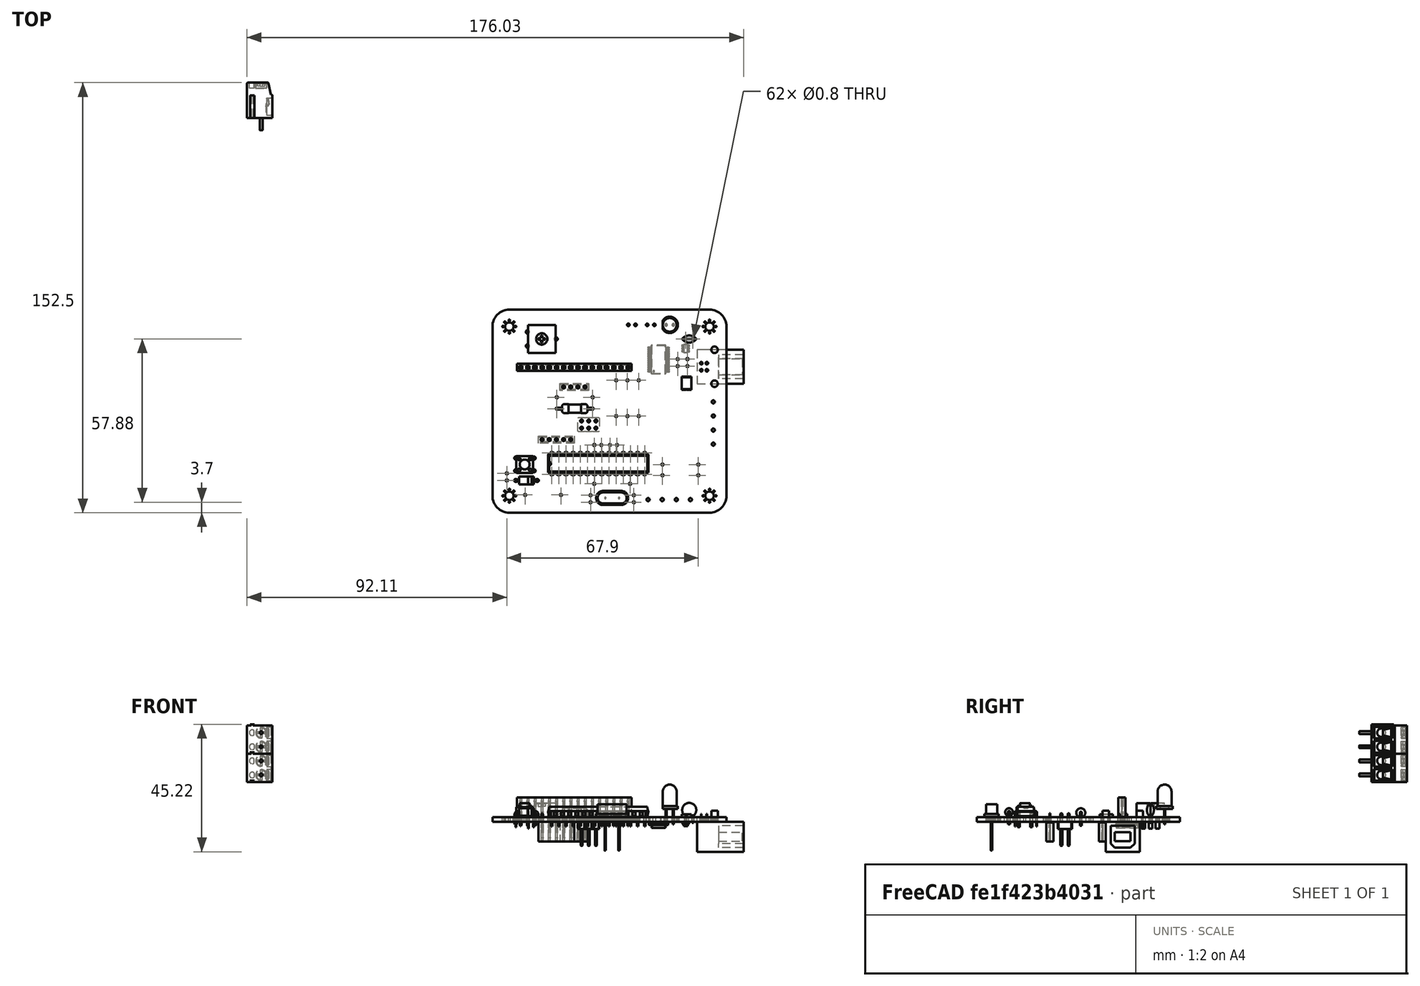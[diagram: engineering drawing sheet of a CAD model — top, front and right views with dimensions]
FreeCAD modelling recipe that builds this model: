
FCSTD DOCUMENT  (FreeCAD 0.19R22665 (Git))
Label: pcb_board
License: All rights reserved
LicenseURL: http://en.wikipedia.org/wiki/All_rights_reserved
objects: App::Link×20, Part::Feature×19, App::Part×6, PartDesign::CoordinateSystem×3, Sketcher::SketchObject×1
note: 23 computed .brp shape members not serialized (recipe doc carries the construction recipe); baked Part::Feature solids carry a one-line shape summary decoded from their .brp

FEATURE [PartDesign::CoordinateSystem] Local_CS_8929
  AttacherType = Attacher::AttachEngine3D
FEATURE [Part::Feature] Pcb_8929
  shape: bbox 83 x 72 x 1.6 mm, 170 faces (baked)
FEATURE [Sketcher::SketchObject] PCB_Sketch_8929
  sketch-geometry (8):
    g0: LineSegment StartX=93 StartY=-68 StartZ=0 EndX=164 EndY=-68 EndZ=0
    g1: LineSegment StartX=170 StartY=-134 StartZ=0 EndX=170 EndY=-74 EndZ=0
    g2: LineSegment StartX=93 StartY=-140 StartZ=0 EndX=164 EndY=-140 EndZ=0
    g3: LineSegment StartX=87 StartY=-74 StartZ=0 EndX=87 EndY=-134 EndZ=0
    g4: ArcOfCircle CenterX=164 CenterY=-74 CenterZ=0 NormalX=0 NormalY=0 NormalZ=1 AngleXU=0 Radius=6 StartAngle=0 EndAngle=1.5708
    g5: ArcOfCircle CenterX=93 CenterY=-134 CenterZ=0 NormalX=0 NormalY=0 NormalZ=1 AngleXU=0 Radius=6 StartAngle=3.14159 EndAngle=4.71239
    g6: ArcOfCircle CenterX=164 CenterY=-134 CenterZ=0 NormalX=0 NormalY=0 NormalZ=1 AngleXU=0 Radius=6 StartAngle=4.71239 EndAngle=6.28319
    g7: ArcOfCircle CenterX=93 CenterY=-74 CenterZ=0 NormalX=0 NormalY=0 NormalZ=1 AngleXU=0 Radius=6 StartAngle=1.5708 EndAngle=3.14159
  constraints (8):
    c: Coincident(g3,g5)
    c: Coincident(g3,g7)
    c: Coincident(g2,g5)
    c: Coincident(g0,g7)
    c: Coincident(g2,g6)
    c: Coincident(g0,g4)
    c: Coincident(g1,g6)
    c: Coincident(g1,g4)
FEATURE [App::Part] Board_Geoms_8929
  Group = -> [Local_CS_8929,Pcb_8929,PCB_Sketch_8929]
  Origin = -> Origin
FEATURE [Part::Feature] Shape  label="J6_PinSocket_1x04_P254mm_Vertical_5FCA8662"
  Placement = pos=(112.235,-95.42,-1.6) rot=(0.707107,-0.707107,0;3.14159rad)
  shape: bbox 10.16 x 2.54 x 10.1 mm, 134 faces (baked)
FEATURE [Part::Feature] Shape001  label="SW1_SW_PUSH_6mm_h5mm_5FCE63C8"
  Placement = pos=(95.29,-120.64,0) rot=(0,0,1;0rad)
  shape: bbox 7.174 x 6 x 8.5 mm, 105 faces (baked)
FEATURE [Part::Feature] Shape002  label="J7_PinSocket_1x05_P254mm_Vertical_5FC31174"
  Placement = pos=(114.78,-114.07,-1.6) rot=(0.707107,0.707107,0;3.14159rad)
  shape: bbox 12.7 x 2.54 x 10.1 mm, 165 faces (baked)
FEATURE [Part::Feature] Shape003  label="RV1_ACP470_5F3BE09B"
  Placement = pos=(104.5,-78.4,0) rot=(0,0,-1;1.5708rad)
  shape: bbox 9.8 x 10 x 9 mm, 36 faces (baked)
FEATURE [App::Link] RV1_ACP470_5F3BE09B_ln_  label="RV1_ACP470_5F3BE09B[2]"
  LinkPlacement = pos=(104.5,-78.4,0) rot=(0,0,-1;1.5708rad)
  LinkedObject = -> Shape003
  Placement = pos=(104.5,-78.4,0) rot=(0,0,-1;1.5708rad)
FEATURE [Part::Feature] Shape004  label="D4_LED_D5.0mm_5FA6C0E4"
  Placement = pos=(148.6,-73.4,0) rot=(0,0,1;0rad)
  shape: bbox 5.4 x 5.8 x 14.1 mm, 16 faces (baked)
FEATURE [Part::Feature] Shape005  label="F1_MF-MSMF050_5FB19120[2]"
  Placement = pos=(155.79,-94.15,0) rot=(0,0,1;1.5708rad)
  shape: bbox 3.41 x 4.73 x 1.1 mm, 14 faces (baked)
FEATURE [App::Link] F1_MF_MSMF050_5FB19120_2__ln_  label="F1_MF-MSMF050_5FB19120[3]"
  LinkPlacement = pos=(155.79,-94.15,0) rot=(0,0,1;1.5708rad)
  LinkedObject = -> Shape005
  Placement = pos=(155.79,-94.15,0) rot=(0,0,1;1.5708rad)
FEATURE [Part::Feature] Shape006  label="U3_SOT_23_6_5FB065DB"
  Placement = pos=(155.53,-81.77,-1.6) rot=(0,1,0;3.14159rad)
  shape: bbox 2.8 x 2.9 x 1.55 mm, 124 faces (baked)
FEATURE [Part::Feature] Shape007  label="D3_D_DO-41_SOD81_P7.62mm_Horizontal_5FCE6338"
  Placement = pos=(102.89,-128.56,0) rot=(0,0,1;3.14159rad)
  shape: bbox 8.618 x 2.72 x 5.71 mm, 15 faces (baked)
FEATURE [Part::Feature] Shape008  label="C5_C_Disc_D50mm_W25mm_P250mm_5FB07593"
  Placement = pos=(158.04,-78.42,0) rot=(0,0,1;3.14159rad)
  shape: bbox 5 x 2.5 x 7.1 mm, 6 faces (baked)
FEATURE [Part::Feature] Part__Feature  label="TB001-500-02P_Green - P"
  shape: bbox 9 x 16.9 x 10.5 mm, 145 faces (baked)
FEATURE [Part::Feature] Part__Feature001  label="TB001-500-02P_Green - P001"
  Placement = pos=(0,0,10) rot=(0,0,1;0rad)
  shape: bbox 9 x 16.9 x 10.5 mm, 145 faces (baked)
FEATURE [App::Part] CUI_DEVICES_TB001_500_P04GR  label="J2_CUI_DEVICES_TB001-500-P04GR_5FCB9D5E[2]"
  Group = -> [Part__Feature,Part__Feature001]
  Origin = -> Origin008
  Placement = pos=(127.21,-130.36,-1.6) rot=(-0.57735,0.57735,-0.57735;2.0944rad)
FEATURE [App::Link] J2_CUI_DEVICES_TB001_500_P04GR_5FCB9D5E_2__ln_  label="J4_CUI_DEVICES_TB001-500-P04GR_5FA8521F[2]"
  LinkPlacement = pos=(160.325,-130.7,-1.6) rot=(-1,0,0;1.5708rad)
  LinkedObject = -> CUI_DEVICES_TB001_500_P04GR
  Placement = pos=(160.325,-130.7,-1.6) rot=(-1,0,0;1.5708rad)
FEATURE [Part::Feature] Shape009  label="J1_usb_b_conn_5FA8DFDA[2]"
  Placement = pos=(161.05,-89.5,-1.6) rot=(1,0,0;3.14159rad)
  shape: bbox 16.5 x 14.34 x 14.52 mm, 44 faces (baked)
FEATURE [Part::Feature] Shape010  label="U1_SSOP_28_53x102mm_P065mm_5FB0862F"
  Placement = pos=(145.91,-85.68,-1.6) rot=(1,0,0;3.14159rad)
  shape: bbox 7.8 x 10.2 x 2.1 mm, 456 faces (baked)
FEATURE [Part::Feature] Shape011  label="Y1_Crystal_5F93F8CD"
  Placement = pos=(129.46,-134.77,0) rot=(0,0,1;3.14159rad)
  shape: bbox 11.35 x 5 x 16.4 mm, 15 faces (baked)
FEATURE [Part::Feature] Shape012  label="U2_DIP-28_W7.62mm_5F8B1761"
  Placement = pos=(108,-126.4,0) rot=(0,0,1;1.5708rad)
  shape: bbox 35.56 x 7.874 x 6.98 mm, 488 faces (baked)
FEATURE [Part::Feature] Shape013  label="J3_PinSocket_1x16_P254mm_Vertical_5FB99047"
  Placement = pos=(97,-88.5,0) rot=(0,0,1;1.5708rad)
  shape: bbox 40.64 x 2.54 x 10.1 mm, 506 faces (baked)
FEATURE [Part::Feature] Shape014  label="J5_PinHeader_2x03_P254mm_Vertical_5FA86B0F"
  Placement = pos=(123.69,-110.005,-1.6) rot=(0.707107,0.707107,0;3.14159rad)
  shape: bbox 7.62 x 5.08 x 11.54 mm, 130 faces (baked)
FEATURE [App::Part] Bot_8929
  Group = -> [Shape,Shape002,Shape006,CUI_DEVICES_TB001_500_P04GR,J2_CUI_DEVICES_TB001_500_P04GR_5FCB9D5E_2__ln_,Shape009,Shape010,Shape014]
  Origin = -> Origin004
FEATURE [App::Link] C5_C_Disc_D50mm_W25mm_P250mm_5FB07593_ln_  label="C1_C_Disc_D50mm_W25mm_P250mm_5FA6C044"
  LinkPlacement = pos=(156.15,-88.02,0) rot=(0,0,1;1.5708rad)
  LinkedObject = -> Shape008
  Placement = pos=(156.15,-88.02,0) rot=(0,0,1;1.5708rad)
FEATURE [App::Link] C5_C_Disc_D50mm_W25mm_P250mm_5FB07593_ln_001  label="C2_C_Disc_D50mm_W25mm_P250mm_5FAFE4E7"
  LinkPlacement = pos=(152.68,-85.53,0) rot=(0,0,-1;1.5708rad)
  LinkedObject = -> Shape008
  Placement = pos=(152.68,-85.53,0) rot=(0,0,-1;1.5708rad)
FEATURE [App::Link] C5_C_Disc_D50mm_W25mm_P250mm_5FB07593_ln_002  label="C3_C_Disc_D50mm_W25mm_P250mm_5FA6C068"
  LinkPlacement = pos=(125.62,-116,0) rot=(0,0,1;3.14159rad)
  LinkedObject = -> Shape008
  Placement = pos=(125.62,-116,0) rot=(0,0,1;3.14159rad)
FEATURE [App::Link] C5_C_Disc_D50mm_W25mm_P250mm_5FB07593_ln_003  label="C4_C_Disc_D50mm_W25mm_P250mm_5FCE6386"
  LinkPlacement = pos=(92.11,-128.56,0) rot=(0,0,1;1.5708rad)
  LinkedObject = -> Shape008
  Placement = pos=(92.11,-128.56,0) rot=(0,0,1;1.5708rad)
FEATURE [App::Link] C5_C_Disc_D50mm_W25mm_P250mm_5FB07593_ln_004  label="C6_C_Disc_D50mm_W25mm_P250mm_5FA6D61D"
  LinkPlacement = pos=(128.67,-116,0) rot=(0,0,1;0rad)
  LinkedObject = -> Shape008
  Placement = pos=(128.67,-116,0) rot=(0,0,1;0rad)
FEATURE [App::Link] C5_C_Disc_D50mm_W25mm_P250mm_5FB07593_ln_005  label="C7_C_Disc_D50mm_W25mm_P250mm_5FA6C09E"
  LinkPlacement = pos=(121.8,-136.3,0) rot=(0,0,1;1.5708rad)
  LinkedObject = -> Shape008
  Placement = pos=(121.8,-136.3,0) rot=(0,0,1;1.5708rad)
FEATURE [App::Link] C5_C_Disc_D50mm_W25mm_P250mm_5FB07593_ln_006  label="C8_C_Disc_D50mm_W25mm_P250mm_5FA6C0B0"
  LinkPlacement = pos=(137.15,-136.3,0) rot=(0,0,1;1.5708rad)
  LinkedObject = -> Shape008
  Placement = pos=(137.15,-136.3,0) rot=(0,0,1;1.5708rad)
FEATURE [App::Link] D4_LED_D5_0mm_5FA6C0E4_ln_  label="D1_LED_D5.0mm_5FCBACB3"
  LinkPlacement = pos=(135.2,-73.4,0) rot=(0,0,1;0rad)
  LinkedObject = -> Shape004
  Placement = pos=(135.2,-73.4,0) rot=(0,0,1;0rad)
FEATURE [App::Link] D4_LED_D5_0mm_5FA6C0E4_ln_001  label="D2_LED_D5.0mm_5FCBAF12"
  LinkPlacement = pos=(141.9,-73.4,0) rot=(0,0,1;0rad)
  LinkedObject = -> Shape004
  Placement = pos=(141.9,-73.4,0) rot=(0,0,1;0rad)
FEATURE [Part::Feature] Shape015  label="R1_R_Axial_DIN0309_L90mm_D32mm_P1270mm_Horizontal_5FCA8AFD"
  Placement = pos=(109.85,-103.11,0) rot=(0,0,1;0rad)
  shape: bbox 13.63 x 3.464 x 6.332 mm, 17 faces (baked)
FEATURE [App::Link] R1_R_Axial_DIN0309_L90mm_D32mm_P1270mm_Horizontal_5FCA8AFD_ln_  label="R2_R_Axial_DIN0309_L90mm_D32mm_P1270mm_Horizontal_5FCA8ABB"
  LinkPlacement = pos=(109.85,-99.065,0) rot=(0,0,1;0rad)
  LinkedObject = -> Shape015
  Placement = pos=(109.85,-99.065,0) rot=(0,0,1;0rad)
FEATURE [App::Link] R1_R_Axial_DIN0309_L90mm_D32mm_P1270mm_Horizontal_5FCA8AFD_ln_001  label="R3_R_Axial_DIN0309_L90mm_D32mm_P1270mm_Horizontal_5FB070BF"
  LinkPlacement = pos=(130.875,-105.765,0) rot=(0,0,1;1.5708rad)
  LinkedObject = -> Shape015
  Placement = pos=(130.875,-105.765,0) rot=(0,0,1;1.5708rad)
FEATURE [App::Link] R1_R_Axial_DIN0309_L90mm_D32mm_P1270mm_Horizontal_5FCA8AFD_ln_002  label="R4_R_Axial_DIN0309_L90mm_D32mm_P1270mm_Horizontal_5FB0707D"
  LinkPlacement = pos=(134.875,-105.765,0) rot=(0,0,1;1.5708rad)
  LinkedObject = -> Shape015
  Placement = pos=(134.875,-105.765,0) rot=(0,0,1;1.5708rad)
FEATURE [App::Link] R1_R_Axial_DIN0309_L90mm_D32mm_P1270mm_Horizontal_5FCA8AFD_ln_003  label="R6_R_Axial_DIN0309_L90mm_D32mm_P1270mm_Horizontal_5FA6C1B1"
  LinkPlacement = pos=(111.3,-133.7,0) rot=(0,0,1;3.14159rad)
  LinkedObject = -> Shape015
  Placement = pos=(111.3,-133.7,0) rot=(0,0,1;3.14159rad)
FEATURE [App::Link] R1_R_Axial_DIN0309_L90mm_D32mm_P1270mm_Horizontal_5FCA8AFD_ln_004  label="R7_R_Axial_DIN0309_L90mm_D32mm_P1270mm_Horizontal_5FA6CB65"
  LinkPlacement = pos=(123.1,-129.75,0) rot=(0,0,1;0rad)
  LinkedObject = -> Shape015
  Placement = pos=(123.1,-129.75,0) rot=(0,0,1;0rad)
FEATURE [App::Link] R1_R_Axial_DIN0309_L90mm_D32mm_P1270mm_Horizontal_5FCA8AFD_ln_005  label="R8_R_Axial_DIN0309_L90mm_D32mm_P1270mm_Horizontal_5FA6F1A2"
  LinkPlacement = pos=(147.31,-122.925,0) rot=(0,0,1;0rad)
  LinkedObject = -> Shape015
  Placement = pos=(147.31,-122.925,0) rot=(0,0,1;0rad)
FEATURE [App::Link] R1_R_Axial_DIN0309_L90mm_D32mm_P1270mm_Horizontal_5FCA8AFD_ln_006  label="R9_R_Axial_DIN0309_L90mm_D32mm_P1270mm_Horizontal_5FB07101"
  LinkPlacement = pos=(138.875,-93.065,0) rot=(0,0,-1;1.5708rad)
  LinkedObject = -> Shape015
  Placement = pos=(138.875,-93.065,0) rot=(0,0,-1;1.5708rad)
FEATURE [App::Link] R1_R_Axial_DIN0309_L90mm_D32mm_P1270mm_Horizontal_5FCA8AFD_ln_007  label="R11_R_Axial_DIN0309_L90mm_D32mm_P1270mm_Horizontal_5FCB9A34"
  LinkPlacement = pos=(160.01,-126.73,0) rot=(0,0,1;3.14159rad)
  LinkedObject = -> Shape015
  Placement = pos=(160.01,-126.73,0) rot=(0,0,1;3.14159rad)
FEATURE [App::Part] Top_8929
  Group = -> [Shape001,Shape003,RV1_ACP470_5F3BE09B_ln_,Shape004,Shape005,F1_MF_MSMF050_5FB19120_2__ln_,Shape007,Shape008,Shape011,Shape012,Shape013,C5_C_Disc_D50mm_W25mm_P250mm_5FB07593_ln_,C5_C_Disc_D50mm_W25mm_P250mm_5FB07593_ln_001,C5_C_Disc_D50mm_W25mm_P250mm_5FB07593_ln_002,C5_C_Disc_D50mm_W25mm_P250mm_5FB07593_ln_003,C5_C_Disc_D50mm_W25mm_P250mm_5FB07593_ln_004,+13 more]
  Origin = -> Origin003
FEATURE [App::Part] Step_Models_8929
  Group = -> [Top_8929,Bot_8929]
  Origin = -> Origin002
FEATURE [PartDesign::CoordinateSystem] LCS_lcd
  AttacherType = Attacher::AttachEngine3D
  MapMode = 7
  Placement = pos=(95.73,-87.23,7) rot=(0,0.707107,0.707107;3.14159rad)
  Support = -> [Shape013]
FEATURE [PartDesign::CoordinateSystem] LCS_box
  AttacherType = Attacher::AttachEngine3D
  MapMode = 11
  Placement = pos=(93,-134,-1.6) rot=(0,0,1;1.5708rad)
  Support = -> [Pcb_8929]
FEATURE [App::Part] Board_8929  label="livello_serbatoio_definitiva"
  Group = -> [Board_Geoms_8929,Step_Models_8929,LCS_lcd,LCS_box]
  Origin = -> Origin001
